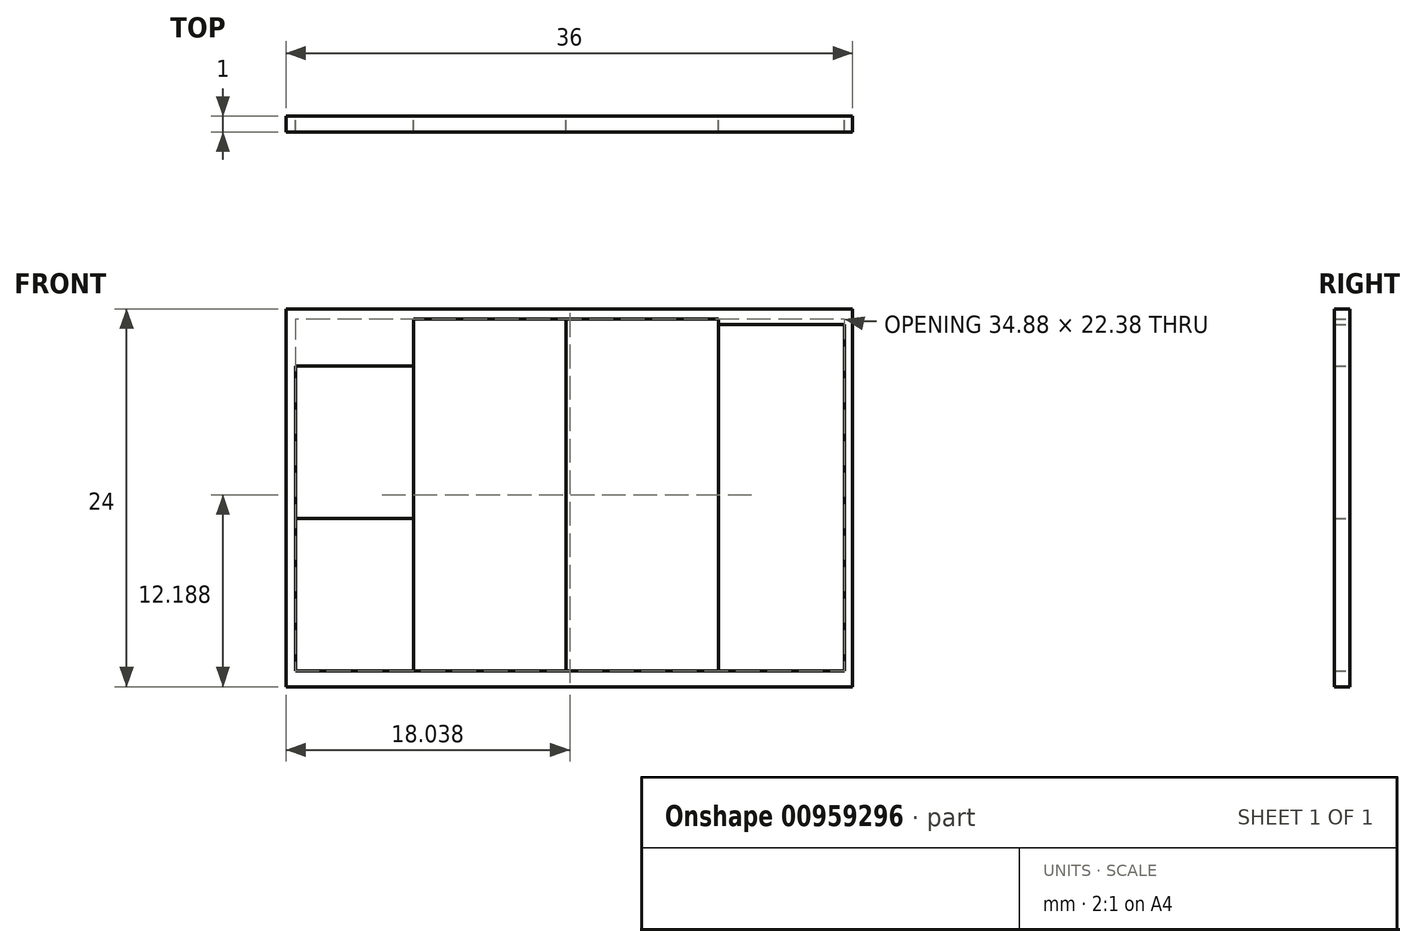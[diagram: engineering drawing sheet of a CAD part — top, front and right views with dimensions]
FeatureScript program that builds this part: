
annotation { "Feature Type Name" : "Feature", "Feature Type Description" : "" }
export const myFeature = defineFeature(function(context is Context, id is Id, definition is map)
    precondition{}
    {
        {
            var Q0;
            Q0=qCreatedBy(makeId("Front.planeOp"),FACE);
            var sketch = newSketch(context, id + "F0", { "sketchPlane" : qUnion([Q0])});
            skLineSegment(sketch, "E0.bottom", {"start": v(0.6, 10.69) * mm, "end": v(8.1, 10.69) * mm});
            skLineSegment(sketch, "E0.top", {"start": v(0.6, 20.37) * mm, "end": v(8.1, 20.37) * mm});
            skLineSegment(sketch, "E0.left", {"start": v(0.6, 10.69) * mm, "end": v(0.6, 20.37) * mm});
            skLineSegment(sketch, "E1.top", {"start": v(8.1, 23.37) * mm, "end": v(17.79, 23.37) * mm});
            skLineSegment(sketch, "E1.left", {"start": v(8.1, 1) * mm, "end": v(8.1, 23.37) * mm});
            skLineSegment(sketch, "E2.1.0.0", {"start": v(17.79, 1) * mm, "end": v(17.79, 23.37) * mm});
            skLineSegment(sketch, "E2.1.0.1", {"start": v(17.79, 23.37) * mm, "end": v(27.47, 23.37) * mm});
            skLineSegment(sketch, "E2.1.0.2", {"start": v(27.47, 1) * mm, "end": v(27.47, 23.37) * mm});
            skLineSegment(sketch, "E3.top", {"start": v(27.47, 23) * mm, "end": v(35.47, 23) * mm});
            skLineSegment(sketch, "E3.right", {"start": v(35.47, 1) * mm, "end": v(35.47, 23) * mm});
            skLineSegment(sketch, "E4.bottom", {"start": v(0, 0) * mm, "end": v(36, 0) * mm});
            skLineSegment(sketch, "E4.top", {"start": v(0, 24) * mm, "end": v(36, 24) * mm});
            skLineSegment(sketch, "E4.left", {"start": v(0, 0) * mm, "end": v(0, 24) * mm});
            skLineSegment(sketch, "E4.right", {"start": v(36, 0) * mm, "end": v(36, 24) * mm});
            skLineSegment(sketch, "E5", {"start": v(8.1, 1) * mm, "end": v(0.6, 1) * mm});
            skLineSegment(sketch, "E6", {"start": v(0.6, 1) * mm, "end": v(0.6, 10.69) * mm});
            skLineSegment(sketch, "E7", {"start": v(8.1, 1) * mm, "end": v(17.79, 1) * mm});
            skLineSegment(sketch, "E8", {"start": v(17.79, 1) * mm, "end": v(27.47, 1) * mm});
            skLineSegment(sketch, "E9", {"start": v(35.47, 1) * mm, "end": v(27.47, 1) * mm});
            skSolve(sketch);
        }
        {
            var Q0;
            {var subQ3=sQuery(id+"F0.wireOp",EDGE,"E0.top");Q0=makeQuery(id+"F0.imprint","IMPRINT",FACE,{"disambiguationData":[TD([[makeQuery(id+"F0.imprint","IMPRINT",EDGE,{"derivedFrom":subQ3}),1.0]])]});}
            extrude(context, id + "F1", {"entities" : qUnion([Q0]), "depth" : 1 * mm, "offsetDistance" : 25 * mm});
        }
        {
            var Q0;
            {var subQ2=sQuery(id+"F0.wireOp",EDGE,"E1.top");Q0=makeQuery(id+"F0.imprint","IMPRINT",FACE,{"disambiguationData":[TD([[makeQuery(id+"F0.imprint","IMPRINT",EDGE,{"derivedFrom":subQ2}),-1.0]])]});}
            extrude(context, id + "F2", {"entities" : qUnion([Q0]), "depth" : 1 * mm, "offsetDistance" : 25 * mm});
        }
        {
            var Q0;
            {var subQ0=sQuery(id+"F0.wireOp",EDGE,"E0.bottom");Q0=makeQuery(id+"F0.imprint","IMPRINT",FACE,{"disambiguationData":[TD([[makeQuery(id+"F0.imprint","IMPRINT",EDGE,{"derivedFrom":subQ0}),1.0]])]});}
            extrude(context, id + "F3", {"entities" : qUnion([Q0]), "depth" : 1 * mm, "offsetDistance" : 25 * mm});
        }
        {
            var Q0;
            {var subQ0=sQuery(id+"F0.wireOp",EDGE,"E0.bottom");Q0=makeQuery(id+"F0.imprint","IMPRINT",FACE,{"disambiguationData":[TD([[makeQuery(id+"F0.imprint","IMPRINT",EDGE,{"derivedFrom":subQ0}),-1.0]])]});}
            extrude(context, id + "F4", {"entities" : qUnion([Q0]), "depth" : 1 * mm, "offsetDistance" : 25 * mm});
        }
        {
            var Q0;
            Q0=makeQuery(id+"F0.imprint","IMPRINT",FACE,{"disambiguationData":[TD([[makeQuery(id+"F0.imprint","IMPRINT",EDGE,{"derivedFrom":sQuery(id+"F0.wireOp",EDGE,"E2.1.0.0")}),-1.0]])]});
            extrude(context, id + "F5", {"entities" : qUnion([Q0]), "depth" : 1 * mm, "offsetDistance" : 25 * mm});
        }
        {
            var Q0;
            {var subQ2=sQuery(id+"F0.wireOp",EDGE,"E3.top");Q0=makeQuery(id+"F0.imprint","IMPRINT",FACE,{"disambiguationData":[TD([[makeQuery(id+"F0.imprint","IMPRINT",EDGE,{"derivedFrom":subQ2}),-1.0]])]});}
            extrude(context, id + "F6", {"entities" : qUnion([Q0]), "depth" : 1 * mm, "offsetDistance" : 25 * mm});
        }
    });
